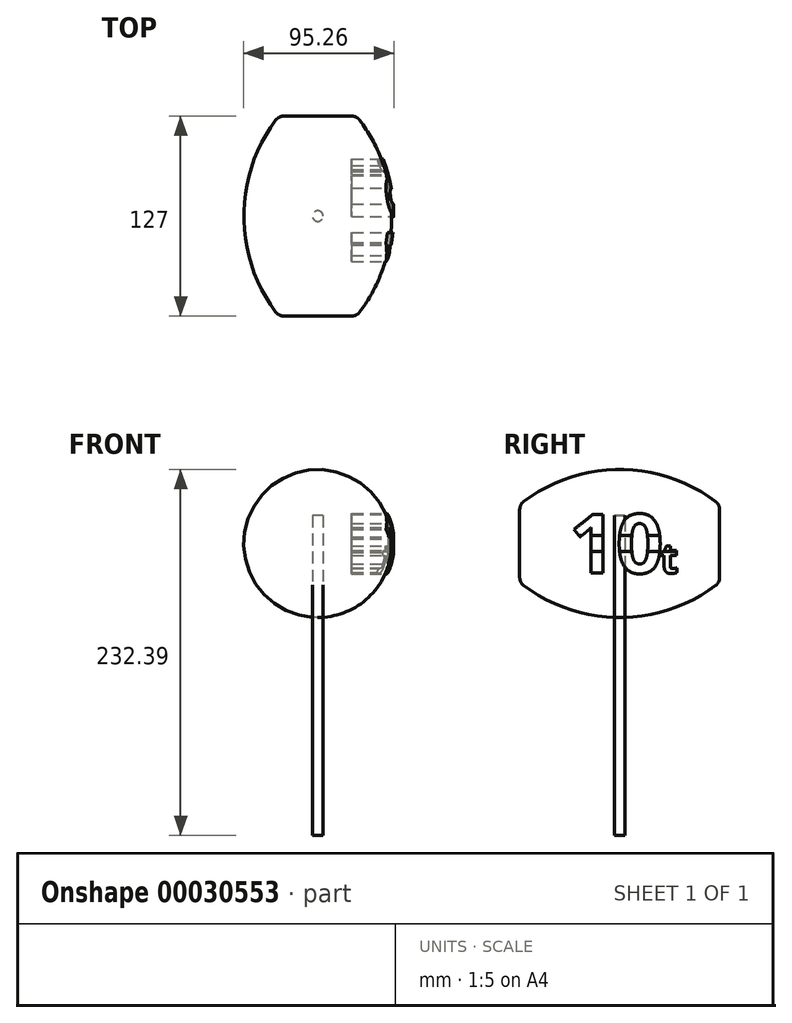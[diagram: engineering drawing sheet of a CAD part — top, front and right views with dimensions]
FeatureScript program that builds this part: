
annotation { "Feature Type Name" : "Feature", "Feature Type Description" : "" }
export const myFeature = defineFeature(function(context is Context, id is Id, definition is map)
    precondition{}
    {
        {
            var Q0;
            Q0=qCreatedBy(makeId("Right.planeOp"),FACE);
            var sketch = newSketch(context, id + "F0", { "sketchPlane" : qUnion([Q0])});
            skLineSegment(sketch, "E0", {"start": v(-54.61, -5.1) * mm, "end": v(-54.61, 16.49) * mm});
            skLineSegment(sketch, "E1.MirrorCS", {"start": v(72.39, -5.1) * mm, "end": v(72.39, 16.49) * mm});
            skPoint(sketch, "E2.start.orphan", {"position": v(0, -20.6) * mm});
            skArc(sketch, "E3", {"start": v(69.85, 21.57) * mm, "mid": v(8.9, 41.89) * mm, "end": v(-52.07, 21.57) * mm});
            skLineSegment(sketch, "E4", {"start": v(-54.61, -5.1) * mm, "end": v(72.4, -5.1) * mm});
            skPoint(sketch, "E5.MirrorCS.end.orphan", {"position": v(-54.61, -18.5) * mm});
            skPoint(sketch, "E6.MirrorCS.end.orphan", {"position": v(72.39, -18.5) * mm});
            skPoint(sketch, "E7.visualSharp", {"position": v(-54.61, 19.6) * mm});
            skArc(sketch, "E7.filletArc", {"start": v(-52.07, 21.57) * mm, "mid": v(-53.94, 19.33) * mm, "end": v(-54.61, 16.49) * mm});
            skPoint(sketch, "E8.visualSharp", {"position": v(72.4, 19.6) * mm});
            skArc(sketch, "E8.filletArc", {"start": v(72.39, 16.49) * mm, "mid": v(71.72, 19.33) * mm, "end": v(69.85, 21.57) * mm});
            skSolve(sketch);
        }
        {
            var Q0;
            Q0 = qSketchRegion(id + "F0", true);
            var Q1;
            Q1=sQuery(id+"F0.wireOp",EDGE,"E4");
            revolve(context, id + "F1", {"entities" : qUnion([Q0]), "axis" : qUnion([Q1]), "revolveType" : RevolveType.FULL});
        }
        {
            var Q0;
            Q0=qCreatedBy(makeId("Right.planeOp"),FACE);
            cPlane(context, id + "F2", {"entities" : qUnion([Q0]), "cplaneType" : CPlaneType.OFFSET, "offset" : 47 * mm, "width" : 152.4 * mm, "height" : 152.4 * mm});
        }
        {
            var Q0;
            Q0=qCreatedBy(id+"F2.planeOp",FACE);
            var sketch = newSketch(context, id + "F3", { "sketchPlane" : qUnion([Q0])});
            skLineSegment(sketch, "E9.0", {"start": v(-52.07, -31.77) * mm, "end": v(-52.07, 21.57) * mm});
            skLineSegment(sketch, "E10.0", {"start": v(69.85, -31.77) * mm, "end": v(69.85, 21.57) * mm});
            skLineSegment(sketch, "E11", {"start": v(-52.07, -5.1) * mm, "end": v(-23.18, -5.1) * mm});
            skLineSegment(sketch, "E12.MirrorCS", {"start": v(69.85, -5.1) * mm, "end": v(40.96, -5.1) * mm});
            skPoint(sketch, "E13.MirrorCS.end.orphan", {"position": v(8.89, -30.9) * mm});
            skPoint(sketch, "E13.MirrorCS.start.orphan", {"position": v(8.89, -5.1) * mm});
            skLineSegment(sketch, "E14.trimOffspring", {"start": v(-23.18, -5.1) * mm, "end": v(-52.07, -5.1) * mm});
            skLineSegment(sketch, "E15.trimOffspring", {"start": v(40.96, -5.1) * mm, "end": v(69.85, -5.1) * mm});
            skPoint(sketch, "E16.end.orphan", {"position": v(-21.03, 20.7) * mm});
            skPoint(sketch, "E16.start.orphan", {"position": v(-23.18, 20.7) * mm});
            skPoint(sketch, "E17.start.orphan", {"position": v(8.89, 20.7) * mm});
            skPoint(sketch, "E18.end.orphan", {"position": v(40.96, 19.5) * mm});
            skPoint(sketch, "E18.start.orphan", {"position": v(40.96, 20.7) * mm});
            skPoint(sketch, "E19.MirrorCS.start.orphan", {"position": v(37.62, -26.84) * mm});
            skText(sketch, "E20", { "text": "10", "fontName": "OpenSans-Bold.ttf"});
            skText(sketch, "E21", { "text": "t", "fontName": "OpenSans-Bold.ttf"});
            skPoint(sketch, "E22.start.orphan", {"position": v(37.62, -23.92) * mm});
            const initialGuessF3  = {"E20": [-0.02318, -0.02392, 1, 0, 0.03764], "E21": [0.03464, -0.02392, 1, 0, 0.01882]};
            skSetInitialGuess(sketch, initialGuessF3);
            skSolve(sketch);
        }
        {
            var Q0;
            Q0 = qSketchRegion(id + "F3", true);
            extrude(context, id + "F4", {"entities" : qUnion([Q0]), "endBound" : BoundingType.SYMMETRIC, "oppositeDirection" : true, "depth" : 50.8 * mm});
        }
        {
            var Q0;
            Q0=qCreatedBy(makeId("Top.planeOp"),FACE);
            var sketch = newSketch(context, id + "F5", { "sketchPlane" : qUnion([Q0])});
            skArc(sketch, "E23", {"start": v(27.94, -52.07) * mm, "mid": v(48.27, 8.89) * mm, "end": v(27.94, 69.85) * mm});
            skLineSegment(sketch, "E24", {"start": v(27.94, -52.07) * mm, "end": v(95.87, -32.3) * mm});
            skLineSegment(sketch, "E25", {"start": v(95.87, -32.3) * mm, "end": v(66.58, 68.35) * mm});
            skLineSegment(sketch, "E26", {"start": v(66.58, 68.35) * mm, "end": v(27.94, 69.85) * mm});
            skPoint(sketch, "E27.0.end.orphan", {"position": v(-26.67, 69.85) * mm});
            skPoint(sketch, "E27.0.start.orphan", {"position": v(26.67, 69.85) * mm});
            skPoint(sketch, "E28.0.end.orphan", {"position": v(-26.67, -52.07) * mm});
            skPoint(sketch, "E29.start.orphan", {"position": v(26.67, -52.07) * mm});
            skSolve(sketch);
        }
        {
            var Q0;
            Q0 = qSketchRegion(id + "F5", true);
            extrude(context, id + "F6", {"entities" : qUnion([Q0]), "operationType" : NewBodyOperationType.REMOVE, "endBound" : BoundingType.SYMMETRIC, "oppositeDirection" : true, "depth" : 254 * mm});
        }
        {
            var Q0;
            Q0=qCreatedBy(makeId("Front.planeOp"),FACE);
            var sketch = newSketch(context, id + "F7", { "sketchPlane" : qUnion([Q0])});
            skArc(sketch, "E30", {"start": v(0, -54.63) * mm, "mid": v(49.53, -5.1) * mm, "end": v(0, 44.43) * mm});
            skPoint(sketch, "E31.start.orphan", {"position": v(0, -52.1) * mm});
            skLineSegment(sketch, "E32", {"start": v(0, -54.63) * mm, "end": v(46.1, -68.23) * mm});
            skLineSegment(sketch, "E33", {"start": v(46.1, -68.23) * mm, "end": v(58.03, 7.17) * mm});
            skLineSegment(sketch, "E34", {"start": v(58.03, 7.17) * mm, "end": v(27.81, 60.5) * mm});
            skLineSegment(sketch, "E35", {"start": v(27.81, 60.5) * mm, "end": v(0, 44.43) * mm});
            skSolve(sketch);
        }
        {
            var Q0;
            Q0=qCreatedBy(makeId("Top.planeOp"),FACE);
            var sketch = newSketch(context, id + "F8", { "sketchPlane" : qUnion([Q0])});
            skLineSegment(sketch, "E36.0", {"start": v(26.67, -52.07) * mm, "end": v(-26.67, -52.07) * mm});
            skLineSegment(sketch, "E37.0", {"start": v(26.67, 69.85) * mm, "end": v(-26.67, 69.85) * mm});
            skArc(sketch, "E38", {"start": v(26.67, -52.07) * mm, "mid": v(47.04, 8.89) * mm, "end": v(26.67, 69.85) * mm});
            skSolve(sketch);
        }
        {
            var Q0;
            Q0=qCreatedBy(makeId("Front.planeOp"),FACE);
            var sketch = newSketch(context, id + "F9", { "sketchPlane" : qUnion([Q0])});
            skArc(sketch, "E39", {"start": v(0, -52.1) * mm, "mid": v(46.99, -5.1) * mm, "end": v(0, 41.89) * mm});
            skSolve(sketch);
        }
        {
            var Q0;
            Q0=makeQuery(id+"F7.imprint","IMPRINT",FACE,{"disambiguationData":[TD([[makeQuery(id+"F7.imprint","IMPRINT",EDGE,{"derivedFrom":sQuery(id+"F7.wireOp",EDGE,"E30")}),-1.0]])]});
            var Q1;
            Q1=sQuery(id+"F8.wireOp",EDGE,"E38");
            sweep(context, id + "F10", {"operationType" : NewBodyOperationType.REMOVE, "profiles" : qUnion([Q0]), "path" : qUnion([Q1])});
        }
        {
            var Q0;
            Q0=qCreatedBy(makeId("Top.planeOp"),FACE);
            var sketch = newSketch(context, id + "F11", { "sketchPlane" : qUnion([Q0])});
            skLineSegment(sketch, "E40.0", {"start": v(46.99, 0) * mm, "end": v(0, 0) * mm});
            skLineSegment(sketch, "E41.0", {"start": v(26.67, -52.07) * mm, "end": v(-26.67, -52.07) * mm});
            skArc(sketch, "E42", {"start": v(26.67, -52.07) * mm, "mid": v(40.57, -27.5) * mm, "end": v(46.99, 0) * mm});
            skSolve(sketch);
        }
        {
            var Q0;
            Q0 = qSketchRegion(id + "F7", true);
            var Q1;
            Q1=sQuery(id+"F11.wireOp",EDGE,"E42");
            sweep(context, id + "F12", {"operationType" : NewBodyOperationType.REMOVE, "profiles" : qUnion([Q0]), "path" : qUnion([Q1])});
        }
        {
            var Q0;
            Q0 = qSketchRegion(id + "F5", true);
            var Q1;
            Q1=sQuery(id+"F9.wireOp",EDGE,"E39");
            sweep(context, id + "F13", {"operationType" : NewBodyOperationType.REMOVE, "profiles" : qUnion([Q0]), "path" : qUnion([Q1])});
        }
        {
            var Q0;
            Q0=qCreatedBy(makeId("Front.planeOp"),FACE);
            var sketch = newSketch(context, id + "F14", { "sketchPlane" : qUnion([Q0])});
            skArc(sketch, "E43", {"start": v(46.99, -5.37) * mm, "mid": v(0.8, 41.88) * mm, "end": v(-46.97, -3.8) * mm});
            skArc(sketch, "E44", {"start": v(46.99, -5.37) * mm, "mid": v(33.39, 28.1) * mm, "end": v(0, 41.89) * mm});
            skSolve(sketch);
        }
        {
            var Q0;
            Q0 = qSketchRegion(id + "F5", true);
            var Q1;
            Q1=sQuery(id+"F14.wireOp",EDGE,"E44");
            sweep(context, id + "F15", {"operationType" : NewBodyOperationType.REMOVE, "profiles" : qUnion([Q0]), "path" : qUnion([Q1])});
        }
        {
            var Q0;
            Q0=qCreatedBy(makeId("Top.planeOp"),FACE);
            cPlane(context, id + "F16", {"entities" : qUnion([Q0]), "cplaneType" : CPlaneType.OFFSET, "offset" : 190.5 * mm, "oppositeDirection" : true, "width" : 152.4 * mm, "height" : 152.4 * mm});
        }
        {
            var Q0;
            Q0=qCreatedBy(id+"F16.planeOp",FACE);
            var sketch = newSketch(context, id + "F17", { "sketchPlane" : qUnion([Q0])});
            skLineSegment(sketch, "E45.0", {"start": v(26.67, -52.07) * mm, "end": v(-26.67, -52.07) * mm});
            skLineSegment(sketch, "E46.0", {"start": v(26.67, 69.85) * mm, "end": v(-26.67, 69.85) * mm});
            skLineSegment(sketch, "E47", {"start": v(0, -52.07) * mm, "end": v(0, 69.85) * mm});
            skCircle(sketch, "E48", {"center": v(0, 8.89) * mm, "radius": 3.37 * mm});
            skSolve(sketch);
        }
        {
            var Q0;
            Q0 = qSketchRegion(id + "F17", true);
            extrude(context, id + "F18", {"entities" : qUnion([Q0]), "depth" : 203.2 * mm});
        }
    });
